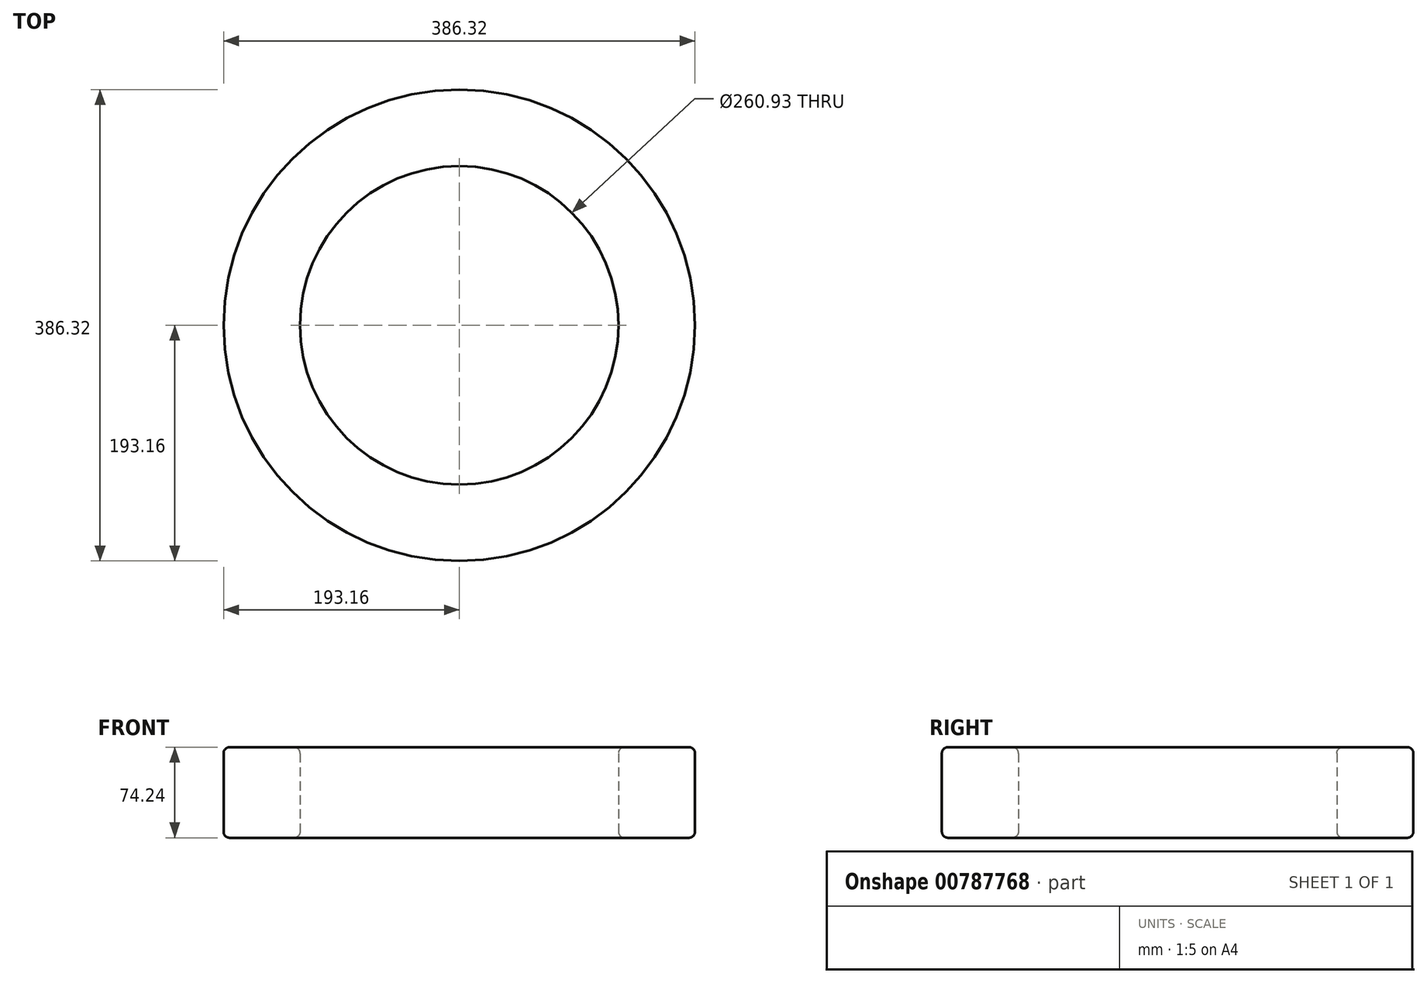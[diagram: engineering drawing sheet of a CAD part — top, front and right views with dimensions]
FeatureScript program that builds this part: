
annotation { "Feature Type Name" : "Feature", "Feature Type Description" : "" }
export const myFeature = defineFeature(function(context is Context, id is Id, definition is map)
    precondition{}
    {
        {
            var Q0;
            Q0=qCreatedBy(makeId("Top.planeOp"),FACE);
            var sketch = newSketch(context, id + "F0", { "sketchPlane" : qUnion([Q0])});
            skCircle(sketch, "E0", {"center": v(0, 0) * mm, "radius": 130.46 * mm});
            skCircle(sketch, "E1", {"center": v(0, 0) * mm, "radius": 191.8 * mm});
            skCircle(sketch, "E2", {"center": v(0, 0) * mm, "radius": 128.9 * mm});
            skCircle(sketch, "E3", {"center": v(0, 0) * mm, "radius": 193.16 * mm});
            skSolve(sketch);
        }
        {
            var Q0;
            Q0 = qSketchRegion(id + "F0", true);
            var Q1;
            Q1=makeQuery(id+"F0.imprint","IMPRINT",FACE,{"disambiguationData":[TD([[makeQuery(id+"F0.imprint","IMPRINT",EDGE,{"derivedFrom":sQuery(id+"F0.wireOp",EDGE,"E0")}),-1.0]])]});
            extrude(context, id + "F1", {"entities" : qUnion([Q0, Q1]), "depth" : 74.24 * mm, "offsetDistance" : 25 * mm});
        }
        {
            var Q0;
            Q0=makeQuery(id+"F1.opExtrude","CAP_FACE",FACE,{"disambiguationData":[OSD([sQuery(id+"F0.wireOp",EDGE,"E0"),sQuery(id+"F0.wireOp",EDGE,"E3")])],"isStart":true});
            var sketch = newSketch(context, id + "F2", { "sketchPlane" : qUnion([Q0])});
            skLineSegment(sketch, "E4", {"start": v(0, 0) * mm, "end": v(130.46, 0) * mm});
            skLineSegment(sketch, "E5", {"start": v(130.46, 0) * mm, "end": v(-77.48, 0) * mm});
            skLineSegment(sketch, "E6", {"start": v(-77.48, 0) * mm, "end": v(-130.46, 0) * mm});
            skLineSegment(sketch, "E7", {"start": v(-130.46, 0) * mm, "end": v(0, 0) * mm});
            skLineSegment(sketch, "E8", {"start": v(0, 0) * mm, "end": v(0, -130.46) * mm});
            skLineSegment(sketch, "E9", {"start": v(0, -130.46) * mm, "end": v(0, 130.46) * mm});
            skLineSegment(sketch, "E10", {"start": v(0, 130.46) * mm, "end": v(0, 0) * mm});
            skLineSegment(sketch, "E11", {"start": v(0, 0) * mm, "end": v(-130.46, 0) * mm});
            skLineSegment(sketch, "E12", {"start": v(-42.49, 0) * mm, "end": v(-109.23, -71.33) * mm});
            skLineSegment(sketch, "E13", {"start": v(-109.23, -71.33) * mm, "end": v(-68.95, -110.75) * mm});
            skLineSegment(sketch, "E14", {"start": v(-68.95, -110.75) * mm, "end": v(0, -42.36) * mm});
            skLineSegment(sketch, "E15", {"start": v(0, -42.36) * mm, "end": v(68.26, -111.18) * mm});
            skLineSegment(sketch, "E16", {"start": v(68.26, -111.18) * mm, "end": v(110.62, -69.16) * mm});
            skLineSegment(sketch, "E17", {"start": v(110.62, -69.16) * mm, "end": v(42.02, 0) * mm});
            skLineSegment(sketch, "E18", {"start": v(42.02, 0) * mm, "end": v(111.05, 68.47) * mm});
            skLineSegment(sketch, "E19", {"start": v(111.05, 68.47) * mm, "end": v(69.37, 110.5) * mm});
            skLineSegment(sketch, "E20", {"start": v(69.37, 110.5) * mm, "end": v(0, 41.68) * mm});
            skLineSegment(sketch, "E21", {"start": v(0, 41.68) * mm, "end": v(-68.68, 110.92) * mm});
            skLineSegment(sketch, "E22", {"start": v(-68.68, 110.92) * mm, "end": v(-110.36, 69.58) * mm});
            skLineSegment(sketch, "E23", {"start": v(-110.36, 69.58) * mm, "end": v(-42.49, 0) * mm});
            skSolve(sketch);
        }
        {
            var Q0;
            {var subQ4=sQuery(id+"F2.wireOp",EDGE,"E15");Q0=makeQuery(id+"F2.imprint","IMPRINT",FACE,{"disambiguationData":[TD([[makeQuery(id+"F2.imprint","IMPRINT",EDGE,{"derivedFrom":subQ4}),1.0]])]});}
            var sketch = newSketch(context, id + "F3", { "sketchPlane" : qUnion([Q0])});
            skLineSegment(sketch, "E24", {"start": v(0, -37.26) * mm, "end": v(70.69, -105.84) * mm});
            skLineSegment(sketch, "E25", {"start": v(70.69, -105.84) * mm, "end": v(104.06, -71.44) * mm});
            skLineSegment(sketch, "E26", {"start": v(104.06, -71.44) * mm, "end": v(30.43, 0) * mm});
            skLineSegment(sketch, "E27", {"start": v(30.43, 0) * mm, "end": v(102.55, 74.34) * mm});
            skLineSegment(sketch, "E28", {"start": v(102.55, 74.34) * mm, "end": v(73.35, 102.66) * mm});
            skLineSegment(sketch, "E29", {"start": v(73.35, 102.66) * mm, "end": v(0, 27.05) * mm});
            skLineSegment(sketch, "E30", {"start": v(0, 27.05) * mm, "end": v(-74.46, 99.3) * mm});
            skLineSegment(sketch, "E31", {"start": v(-74.46, 99.3) * mm, "end": v(-102.83, 70.06) * mm});
            skLineSegment(sketch, "E32", {"start": v(-102.83, 70.06) * mm, "end": v(-30.62, 0) * mm});
            skLineSegment(sketch, "E33", {"start": v(-30.62, 0) * mm, "end": v(-100.58, -72.11) * mm});
            skLineSegment(sketch, "E34", {"start": v(-100.58, -72.11) * mm, "end": v(-69.36, -102.4) * mm});
            skLineSegment(sketch, "E35", {"start": v(-69.36, -102.4) * mm, "end": v(0, -37.26) * mm});
            skSolve(sketch);
        }
        {
            var Q0;
            Q0=sQuery(id+"F2.wireOp",EDGE,"E15");
            var Q1;
            Q1=sQuery(id+"F2.wireOp",EDGE,"E19");
            var Q2;
            Q2=sQuery(id+"F2.wireOp",EDGE,"E14");
            var Q3;
            Q3=sQuery(id+"F2.wireOp",EDGE,"E17");
            var Q4;
            Q4=sQuery(id+"F2.wireOp",EDGE,"E13");
            var Q5;
            Q5=sQuery(id+"F2.wireOp",EDGE,"E22");
            var Q6;
            Q6=sQuery(id+"F2.wireOp",EDGE,"E23");
            var Q7;
            Q7=sQuery(id+"F2.wireOp",EDGE,"E12");
            var Q8;
            Q8=sQuery(id+"F2.wireOp",EDGE,"E21");
            var Q9;
            Q9=sQuery(id+"F2.wireOp",EDGE,"E20");
            var Q10;
            Q10=sQuery(id+"F2.wireOp",EDGE,"E16");
            var Q11;
            Q11=sQuery(id+"F2.wireOp",EDGE,"E18");
            extrude(context, id + "F4", {"bodyType" : ToolBodyType.SURFACE, "surfaceEntities" : qUnion([Q0, Q1, Q2, Q3, Q4, Q5, Q6, Q7, Q8, Q9, Q10, Q11]), "depth" : 5 * mm, "offsetDistance" : 25 * mm});
        }
        {
            var Q0;
            Q0=makeQuery(id+"F1.opExtrude","CAP_EDGE",EDGE,{"disambiguationData":[OSD([sQuery(id+"F0.wireOp",EDGE,"E3")])],"isStart":false});
            var Q1;
            Q1=makeQuery(id+"F1.opExtrude","CAP_EDGE",EDGE,{"disambiguationData":[OSD([sQuery(id+"F0.wireOp",EDGE,"E0")])],"isStart":true});
            var Q2;
            Q2=makeQuery(id+"F1.opExtrude","CAP_EDGE",EDGE,{"disambiguationData":[OSD([sQuery(id+"F0.wireOp",EDGE,"E3")])],"isStart":true});
            var Q3;
            Q3=makeQuery(id+"F1.opExtrude","CAP_EDGE",EDGE,{"disambiguationData":[OSD([sQuery(id+"F0.wireOp",EDGE,"E0")])],"isStart":false});
            fillet(context, id + "F5", {"entities" : qUnion([Q0, Q1, Q2, Q3]), "radius" : 5 * mm, "tangentPropagation" : true, "allowEdgeOverflow" : false});
        }
    });
